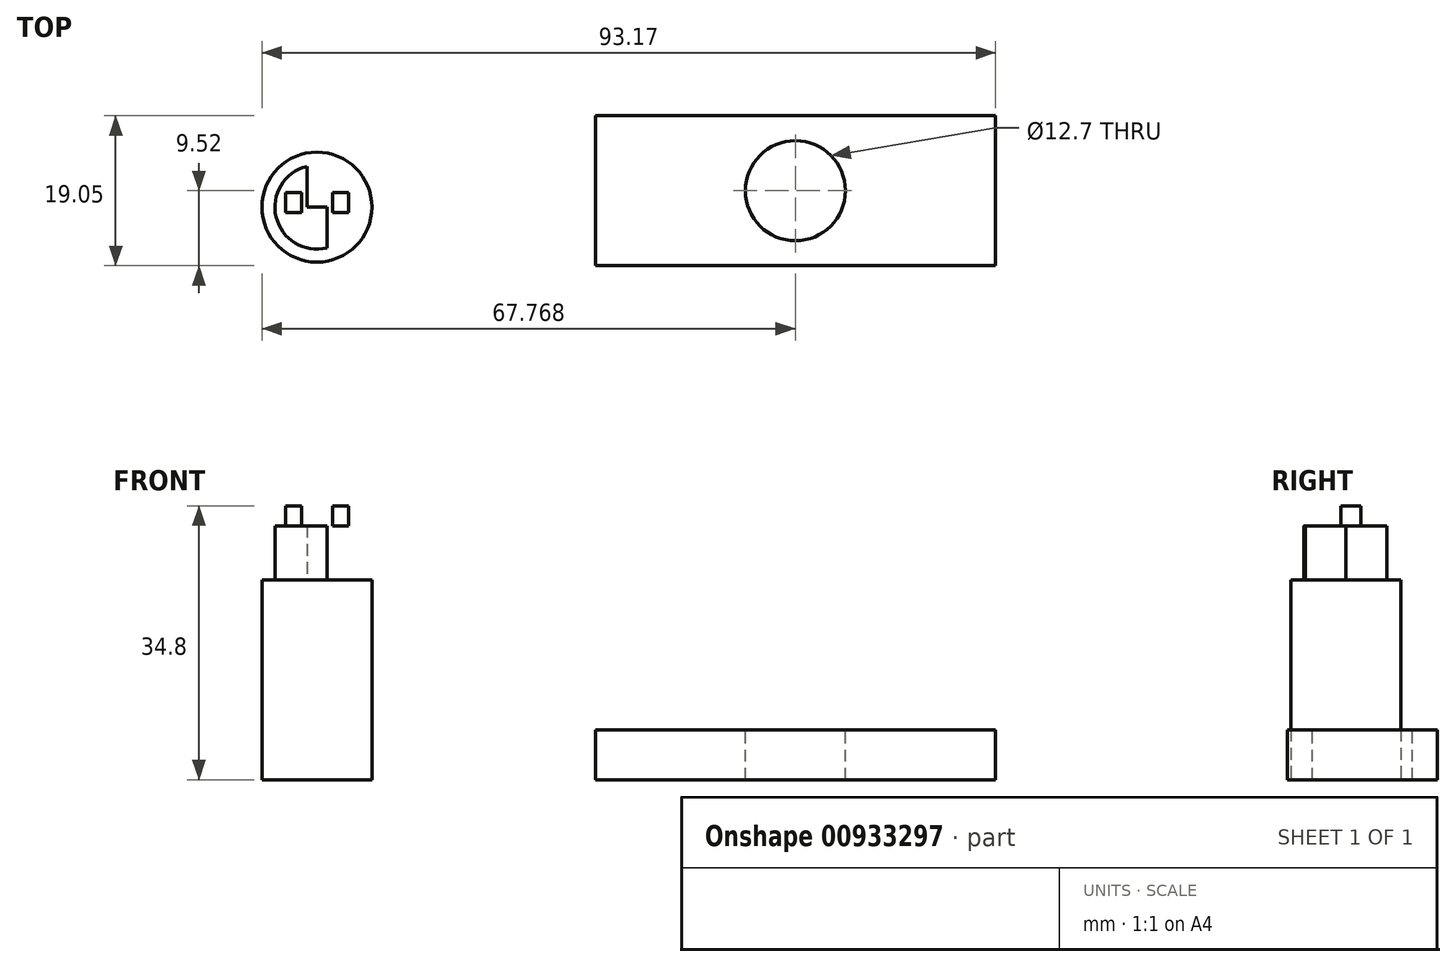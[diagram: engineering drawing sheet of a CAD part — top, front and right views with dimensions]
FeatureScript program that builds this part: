
annotation { "Feature Type Name" : "Feature", "Feature Type Description" : "" }
export const myFeature = defineFeature(function(context is Context, id is Id, definition is map)
    precondition{}
    {
        {
            var Q0;
            Q0=qCreatedBy(makeId("Top.planeOp"),FACE);
            var sketch = newSketch(context, id + "F0", { "sketchPlane" : qUnion([Q0])});
            skLineSegment(sketch, "E0", {"start": v(-13.58, 17.54) * mm, "end": v(37.22, 17.54) * mm});
            skLineSegment(sketch, "E1", {"start": v(37.22, 17.54) * mm, "end": v(37.22, -1.51) * mm});
            skLineSegment(sketch, "E2", {"start": v(37.22, -1.51) * mm, "end": v(-13.58, -1.51) * mm});
            skLineSegment(sketch, "E3", {"start": v(-13.58, -1.51) * mm, "end": v(-13.58, 17.54) * mm});
            skSolve(sketch);
        }
        {
            var Q0;
            Q0 = qSketchRegion(id + "F0", true);
            extrude(context, id + "F1", {"entities" : qUnion([Q0]), "depth" : 6.35 * mm, "offsetDistance" : 25.4 * mm});
        }
        {
            var Q0;
            Q0=makeQuery(id+"F1.opExtrude","CAP_FACE",FACE,{"disambiguationData":[OSD([sQuery(id+"F0.wireOp",EDGE,"E0"),sQuery(id+"F0.wireOp",EDGE,"E1"),sQuery(id+"F0.wireOp",EDGE,"E2"),sQuery(id+"F0.wireOp",EDGE,"E3")])],"isStart":false});
            var sketch = newSketch(context, id + "F2", { "sketchPlane" : qUnion([Q0])});
            skCircle(sketch, "E4", {"center": v(11.82, 8.01) * mm, "radius": 6.35 * mm});
            skSolve(sketch);
        }
        {
            var Q0;
            Q0 = qSketchRegion(id + "F2", true);
            extrude(context, id + "F3", {"entities" : qUnion([Q0]), "operationType" : NewBodyOperationType.REMOVE, "oppositeDirection" : true, "depth" : 25.4 * mm, "offsetDistance" : 25.4 * mm});
        }
        {
            var Q0;
            Q0=qCreatedBy(makeId("Top.planeOp"),FACE);
            var sketch = newSketch(context, id + "F4", { "sketchPlane" : qUnion([Q0])});
            skCircle(sketch, "E5", {"center": v(-48.96, 5.94) * mm, "radius": 6.99 * mm});
            skSolve(sketch);
        }
        {
            var Q0;
            Q0 = qSketchRegion(id + "F4", true);
            extrude(context, id + "F5", {"entities" : qUnion([Q0]), "depth" : 25.4 * mm, "offsetDistance" : 25.4 * mm});
        }
        {
            var Q0;
            Q0=makeQuery(id+"F5.opExtrude","CAP_FACE",FACE,{"disambiguationData":[OSD([sQuery(id+"F4.wireOp",EDGE,"E5")])],"isStart":false});
            var sketch = newSketch(context, id + "F6", { "sketchPlane" : qUnion([Q0])});
            skCircle(sketch, "E6", {"center": v(-48.96, 5.94) * mm, "radius": 5.33 * mm});
            skLineSegment(sketch, "E7", {"start": v(-48.96, 5.94) * mm, "end": v(-50.23, 5.94) * mm});
            skLineSegment(sketch, "E8", {"start": v(-50.23, 5.94) * mm, "end": v(-48.96, 5.94) * mm});
            skLineSegment(sketch, "E9", {"start": v(-47.7, 5.94) * mm, "end": v(-48.96, 5.94) * mm});
            skLineSegment(sketch, "E10", {"start": v(-50.23, 5.94) * mm, "end": v(-50.23, 11.12) * mm});
            skLineSegment(sketch, "E11", {"start": v(-47.7, 5.94) * mm, "end": v(-47.7, 11.12) * mm});
            skLineSegment(sketch, "E12", {"start": v(-47.7, 11.12) * mm, "end": v(-47.7, 0.75) * mm});
            skLineSegment(sketch, "E13", {"start": v(-50.23, 5.94) * mm, "end": v(-50.23, 0.75) * mm});
            skSolve(sketch);
        }
        {
            var Q0;
            {var subQ0=sQuery(id+"F6.wireOp",EDGE,"E12");var subQ1=sQuery(id+"F6.wireOp",EDGE,"E6");var subQ2=makeQuery(id+"F6.imprint","INTERSECT",VERTEX,{"disambiguationData":[OD(0.0)],"derivedFrom":[subQ1,subQ0]});Q0=makeQuery(id+"F6.imprint","IMPRINT",FACE,{"disambiguationData":[TD([[makeQuery(id+"F6.imprint","IMPRINT",EDGE,{"disambiguationData":[TD([[subQ2,1.0]])],"derivedFrom":subQ1}),1.0]])]});}
            var Q1;
            {var subQ0=sQuery(id+"F6.wireOp",EDGE,"E10");Q1=makeQuery(id+"F6.imprint","IMPRINT",FACE,{"disambiguationData":[TD([[makeQuery(id+"F6.imprint","IMPRINT",EDGE,{"derivedFrom":subQ0}),1.0]])]});}
            extrude(context, id + "F7", {"entities" : qUnion([Q0, Q1]), "operationType" : NewBodyOperationType.ADD, "depth" : 6.86 * mm, "offsetDistance" : 25.4 * mm});
        }
        {
            var Q0;
            Q0=makeQuery(id+"F7.opExtrude","CAP_FACE",FACE,{"disambiguationData":[OSD([sQuery(id+"F6.wireOp",EDGE,"E6"),sQuery(id+"F6.wireOp",EDGE,"E12")])],"isStart":false});
            var sketch = newSketch(context, id + "F8", { "sketchPlane" : qUnion([Q0])});
            skLineSegment(sketch, "E14", {"start": v(-46.96, 7.8) * mm, "end": v(-44.93, 7.8) * mm});
            skLineSegment(sketch, "E15", {"start": v(-44.93, 7.8) * mm, "end": v(-44.93, 5.25) * mm});
            skLineSegment(sketch, "E16", {"start": v(-46.96, 5.25) * mm, "end": v(-46.96, 7.8) * mm});
            skLineSegment(sketch, "E17", {"start": v(-44.93, 5.25) * mm, "end": v(-46.96, 5.25) * mm});
            skLineSegment(sketch, "E18", {"start": v(-50.94, 7.8) * mm, "end": v(-50.94, 5.25) * mm});
            skLineSegment(sketch, "E19", {"start": v(-50.94, 5.25) * mm, "end": v(-52.97, 5.25) * mm});
            skLineSegment(sketch, "E20", {"start": v(-52.97, 5.25) * mm, "end": v(-52.97, 7.8) * mm});
            skLineSegment(sketch, "E21", {"start": v(-52.97, 7.8) * mm, "end": v(-50.94, 7.8) * mm});
            skSolve(sketch);
        }
        {
            var Q0;
            Q0 = qSketchRegion(id + "F8", true);
            extrude(context, id + "F9", {"entities" : qUnion([Q0]), "operationType" : NewBodyOperationType.ADD, "depth" : 2.54 * mm, "offsetDistance" : 25.4 * mm});
        }
    });
